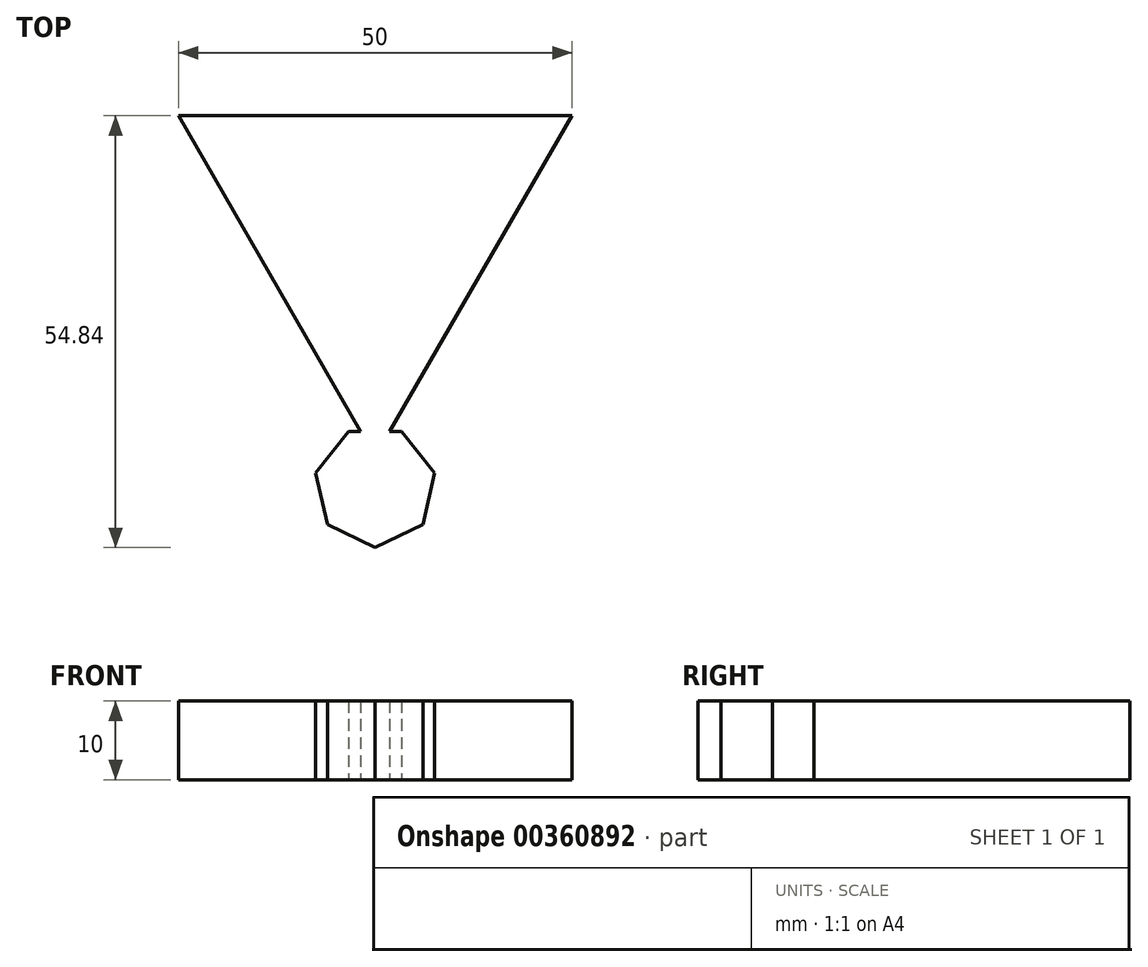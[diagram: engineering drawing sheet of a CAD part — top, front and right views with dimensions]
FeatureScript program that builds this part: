
annotation { "Feature Type Name" : "Feature", "Feature Type Description" : "" }
export const myFeature = defineFeature(function(context is Context, id is Id, definition is map)
    precondition{}
    {
        {
            var Q0;
            Q0=qCreatedBy(makeId("Top.planeOp"),FACE);
            var sketch = newSketch(context, id + "F0", { "sketchPlane" : qUnion([Q0])});
            skCircle(sketch, "E0.cCircle", {"center": v(0, 0) * mm, "radius": 14.43 * mm, "construction": true});
            skLineSegment(sketch, "E0.0", {"start": v(25, 14.43) * mm, "end": v(0, -28.87) * mm});
            skLineSegment(sketch, "E0.1", {"start": v(0, -28.87) * mm, "end": v(-25, 14.43) * mm});
            skLineSegment(sketch, "E0.2", {"start": v(-25, 14.43) * mm, "end": v(25, 14.43) * mm});
            skPoint(sketch, "E0.0.midPoint", {"position": v(12.5, -7.22) * mm});
            skCircle(sketch, "E1.cCircle", {"center": v(0, -32.66) * mm, "radius": 6.99 * mm, "construction": true});
            skLineSegment(sketch, "E1.0", {"start": v(-6.06, -37.5) * mm, "end": v(-7.56, -30.93) * mm});
            skLineSegment(sketch, "E1.1", {"start": v(-7.56, -30.93) * mm, "end": v(-3.36, -25.67) * mm});
            skLineSegment(sketch, "E1.2", {"start": v(-3.36, -25.67) * mm, "end": v(3.36, -25.67) * mm});
            skLineSegment(sketch, "E1.3", {"start": v(3.36, -25.67) * mm, "end": v(7.56, -30.93) * mm});
            skLineSegment(sketch, "E1.4", {"start": v(7.56, -30.93) * mm, "end": v(6.06, -37.5) * mm});
            skLineSegment(sketch, "E1.5", {"start": v(6.06, -37.5) * mm, "end": v(0, -40.41) * mm});
            skLineSegment(sketch, "E1.6", {"start": v(0, -40.41) * mm, "end": v(-6.06, -37.5) * mm});
            skPoint(sketch, "E1.0.midPoint", {"position": v(-6.81, -34.21) * mm});
            skSolve(sketch);
        }
        {
            var Q0;
            Q0 = qSketchRegion(id + "F0", true);
            extrude(context, id + "F1", {"entities" : qUnion([Q0]), "depth" : 10 * mm});
        }
    });
